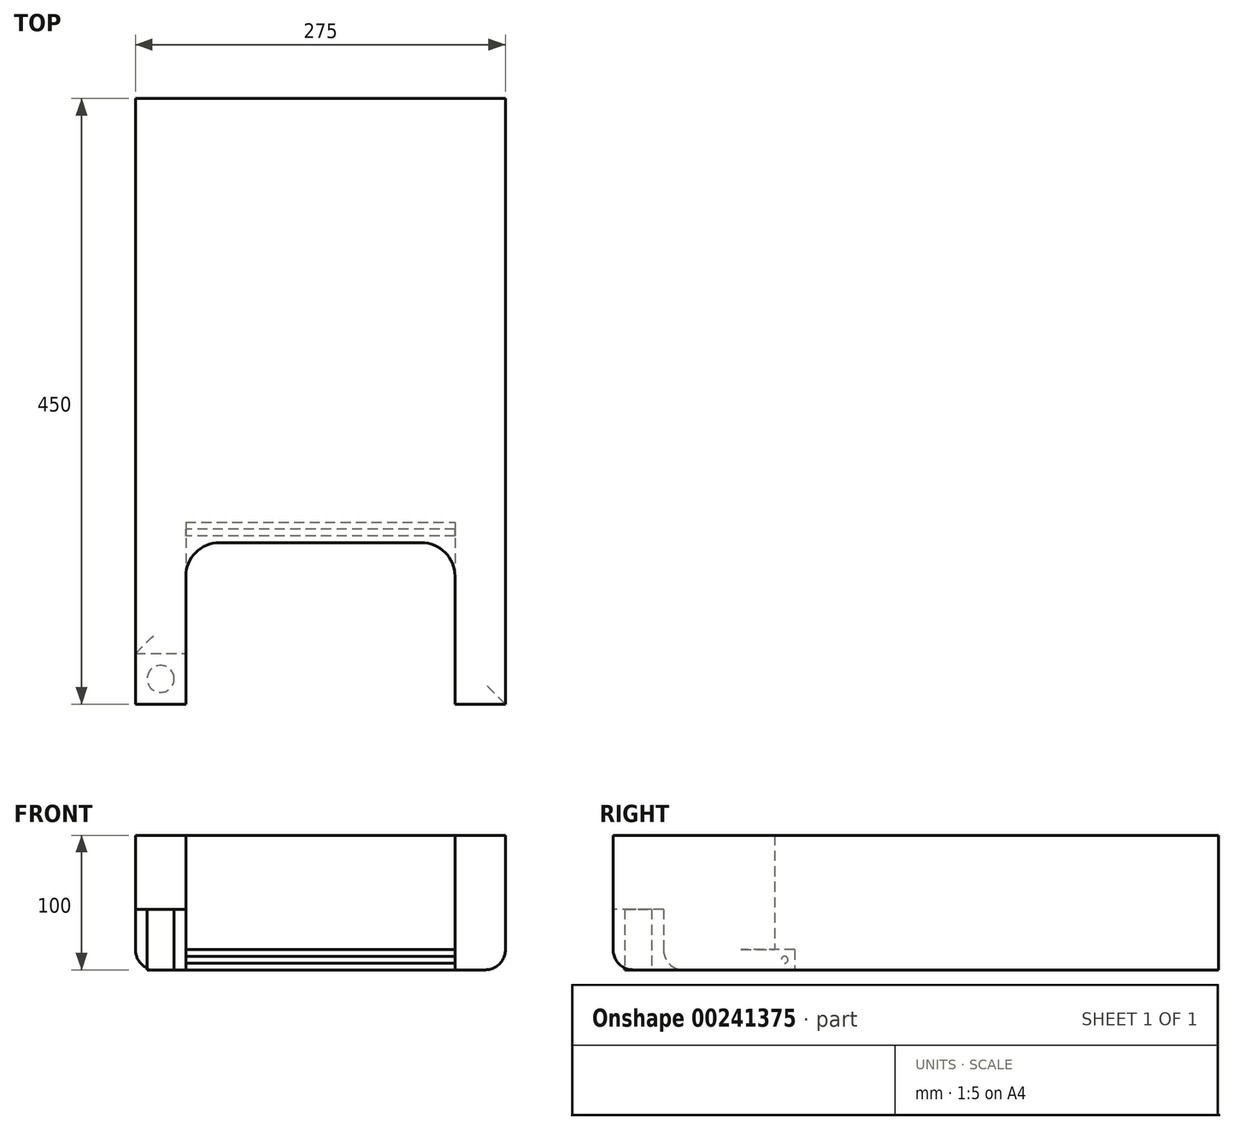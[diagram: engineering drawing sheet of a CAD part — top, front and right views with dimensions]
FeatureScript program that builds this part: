
annotation { "Feature Type Name" : "Feature", "Feature Type Description" : "" }
export const myFeature = defineFeature(function(context is Context, id is Id, definition is map)
    precondition{}
    {
        {
            var Q0;
            Q0=qCreatedBy(makeId("Top.planeOp"),FACE);
            var sketch = newSketch(context, id + "F0", { "sketchPlane" : qUnion([Q0])});
            skLineSegment(sketch, "E0.bottom", {"start": v(-137.5, 225) * mm, "end": v(137.5, 225) * mm});
            skLineSegment(sketch, "E0.top", {"start": v(-137.5, -225) * mm, "end": v(137.5, -225) * mm});
            skLineSegment(sketch, "E0.left", {"start": v(-137.5, 225) * mm, "end": v(-137.5, -225) * mm});
            skLineSegment(sketch, "E0.right", {"start": v(137.5, 225) * mm, "end": v(137.5, -225) * mm});
            skPoint(sketch, "E0.middle", {"position": v(0, 0) * mm});
            skLineSegment(sketch, "E1.bottom", {"start": v(-100, -105) * mm, "end": v(100, -105) * mm});
            skLineSegment(sketch, "E1.top", {"start": v(-100, -225) * mm, "end": v(100, -225) * mm});
            skLineSegment(sketch, "E1.left", {"start": v(-100, -105) * mm, "end": v(-100, -225) * mm});
            skLineSegment(sketch, "E1.right", {"start": v(100, -105) * mm, "end": v(100, -225) * mm});
            skSolve(sketch);
        }
        {
            var Q0;
            Q0=makeQuery(id+"F0.imprint","IMPRINT",FACE,{"disambiguationData":[TD([[makeQuery(id+"F0.imprint","IMPRINT",EDGE,{"derivedFrom":sQuery(id+"F0.wireOp",EDGE,"E0.top")}),1.0]])]});
            extrude(context, id + "F1", {"entities" : qUnion([Q0]), "depth" : 100 * mm});
        }
        {
            var Q0;
            Q0=makeQuery(id+"F1.opExtrude","CAP_FACE",FACE,{"disambiguationData":[OSD([sQuery(id+"F0.wireOp",EDGE,"E0.bottom"),sQuery(id+"F0.wireOp",EDGE,"E0.top"),sQuery(id+"F0.wireOp",EDGE,"E0.left"),sQuery(id+"F0.wireOp",EDGE,"E0.right"),sQuery(id+"F0.wireOp",EDGE,"E1.bottom"),sQuery(id+"F0.wireOp",EDGE,"E1.left"),sQuery(id+"F0.wireOp",EDGE,"E1.right")])],"isStart":true});
            var sketch = newSketch(context, id + "F2", { "sketchPlane" : qUnion([Q0])});
            skLineSegment(sketch, "E2.bottom", {"start": v(-137.5, 225) * mm, "end": v(-100, 225) * mm});
            skLineSegment(sketch, "E2.top", {"start": v(-137.5, 187.5) * mm, "end": v(-100, 187.5) * mm});
            skLineSegment(sketch, "E2.left", {"start": v(-137.5, 225) * mm, "end": v(-137.5, 187.5) * mm});
            skLineSegment(sketch, "E2.right", {"start": v(-100, 225) * mm, "end": v(-100, 187.5) * mm});
            skCircle(sketch, "E3", {"center": v(-118.75, 206.25) * mm, "radius": 10 * mm});
            skPoint(sketch, "E3.centerSnap0", {"position": v(-118.75, 225) * mm});
            skPoint(sketch, "E3.centerSnap1", {"position": v(-137.5, 206.25) * mm});
            skSolve(sketch);
        }
        {
            var Q0;
            Q0=makeQuery(id+"F2.imprint","IMPRINT",FACE,{"disambiguationData":[TD([[makeQuery(id+"F2.imprint","IMPRINT",EDGE,{"derivedFrom":sQuery(id+"F2.wireOp",EDGE,"E2.bottom")}),-1.0]])]});
            extrude(context, id + "F3", {"entities" : qUnion([Q0]), "operationType" : NewBodyOperationType.REMOVE, "oppositeDirection" : true, "depth" : 45 * mm});
        }
        {
            var Q0;
            Q0=makeQuery(id+"F1.opExtrude","SWEPT_FACE",FACE,{"disambiguationData":[OSD([sQuery(id+"F0.wireOp",EDGE,"E1.bottom")])]});
            var sketch = newSketch(context, id + "F4", { "sketchPlane" : qUnion([Q0])});
            skLineSegment(sketch, "E4.bottom", {"start": v(-100, 0) * mm, "end": v(100, 0) * mm});
            skLineSegment(sketch, "E4.top", {"start": v(-100, 15) * mm, "end": v(100, 15) * mm});
            skLineSegment(sketch, "E4.left", {"start": v(-100, 0) * mm, "end": v(-100, 15) * mm});
            skLineSegment(sketch, "E4.right", {"start": v(100, 0) * mm, "end": v(100, 15) * mm});
            skSolve(sketch);
        }
        {
            var Q0;
            Q0 = qSketchRegion(id + "F4", true);
            extrude(context, id + "F5", {"entities" : qUnion([Q0]), "operationType" : NewBodyOperationType.REMOVE, "oppositeDirection" : true, "depth" : 15 * mm});
        }
        {
            var Q0;
            Q0=makeQuery(id+"F5.boolean.opBoolean","MERGE",FACE,{"derivedFrom":[makeQuery(id+"F1.opExtrude","SWEPT_FACE",FACE,{"disambiguationData":[OSD([sQuery(id+"F0.wireOp",EDGE,"E1.left")])]}),makeQuery(id+"F5.opExtrude","SWEPT_FACE",FACE,{"disambiguationData":[OSD([sQuery(id+"F4.wireOp",EDGE,"E4.left")])]})]});
            var sketch = newSketch(context, id + "F6", { "sketchPlane" : qUnion([Q0])});
            skCircle(sketch, "E5", {"center": v(-97.5, 7.5) * mm, "radius": 2.5 * mm});
            skPoint(sketch, "E5.centerSnap0", {"position": v(-90, 7.5) * mm});
            skPoint(sketch, "E5.centerSnap1", {"position": v(-97.5, 15) * mm});
            skSolve(sketch);
        }
        {
            var Q0;
            Q0 = qSketchRegion(id + "F6", true);
            extrude(context, id + "F7", {"entities" : qUnion([Q0]), "operationType" : NewBodyOperationType.ADD, "depth" : 200 * mm});
        }
        {
            var Q0;
            {var subQ0=sQuery(id+"F0.wireOp",EDGE,"E0.top");Q0=makeQuery(id+"F1.opExtrude","CAP_EDGE",EDGE,{"disambiguationData":[OSD([subQ0]),TDD([makeQuery(id+"F0.imprint","IMPRINT",EDGE,{"disambiguationData":[TD([[makeQuery(id+"F0.imprint","INTERSECT",VERTEX,{"derivedFrom":[subQ0,sQuery(id+"F0.wireOp",EDGE,"E0.right")]}),1.0]])],"derivedFrom":subQ0})])],"isStart":true});}
            var Q1;
            Q1=makeQuery(id+"F1.opExtrude","CAP_EDGE",EDGE,{"disambiguationData":[OSD([sQuery(id+"F0.wireOp",EDGE,"E0.right")])],"isStart":true});
            var Q2;
            Q2=makeQuery(id+"F1.opExtrude","CAP_EDGE",EDGE,{"disambiguationData":[OSD([sQuery(id+"F0.wireOp",EDGE,"E0.left")])],"isStart":true});
            var Q3;
            Q3=makeQuery(id+"F3.boolean.opBoolean","COPY",EDGE,{"derivedFrom":makeQuery(id+"F3.opExtrude","CAP_EDGE",EDGE,{"disambiguationData":[OSD([sQuery(id+"F2.wireOp",EDGE,"E2.top")])],"isStart":true})});
            fillet(context, id + "F8", {"entities" : qUnion([Q0, Q1, Q2, Q3]), "radius" : 15 * mm, "tangentPropagation" : true, "allowEdgeOverflow" : false});
        }
        {
            var Q0;
            Q0=makeQuery(id+"F1.opExtrude","SWEPT_EDGE",EDGE,{"disambiguationData":[OSD([sQuery(id+"F0.wireOp",EDGE,"E1.bottom"),sQuery(id+"F0.wireOp",EDGE,"E1.left")])]});
            var Q1;
            Q1=makeQuery(id+"F1.opExtrude","SWEPT_EDGE",EDGE,{"disambiguationData":[OSD([sQuery(id+"F0.wireOp",EDGE,"E1.bottom"),sQuery(id+"F0.wireOp",EDGE,"E1.right")])]});
            fillet(context, id + "F9", {"entities" : qUnion([Q0, Q1]), "radius" : 25 * mm, "tangentPropagation" : true, "allowEdgeOverflow" : false});
        }
    });
